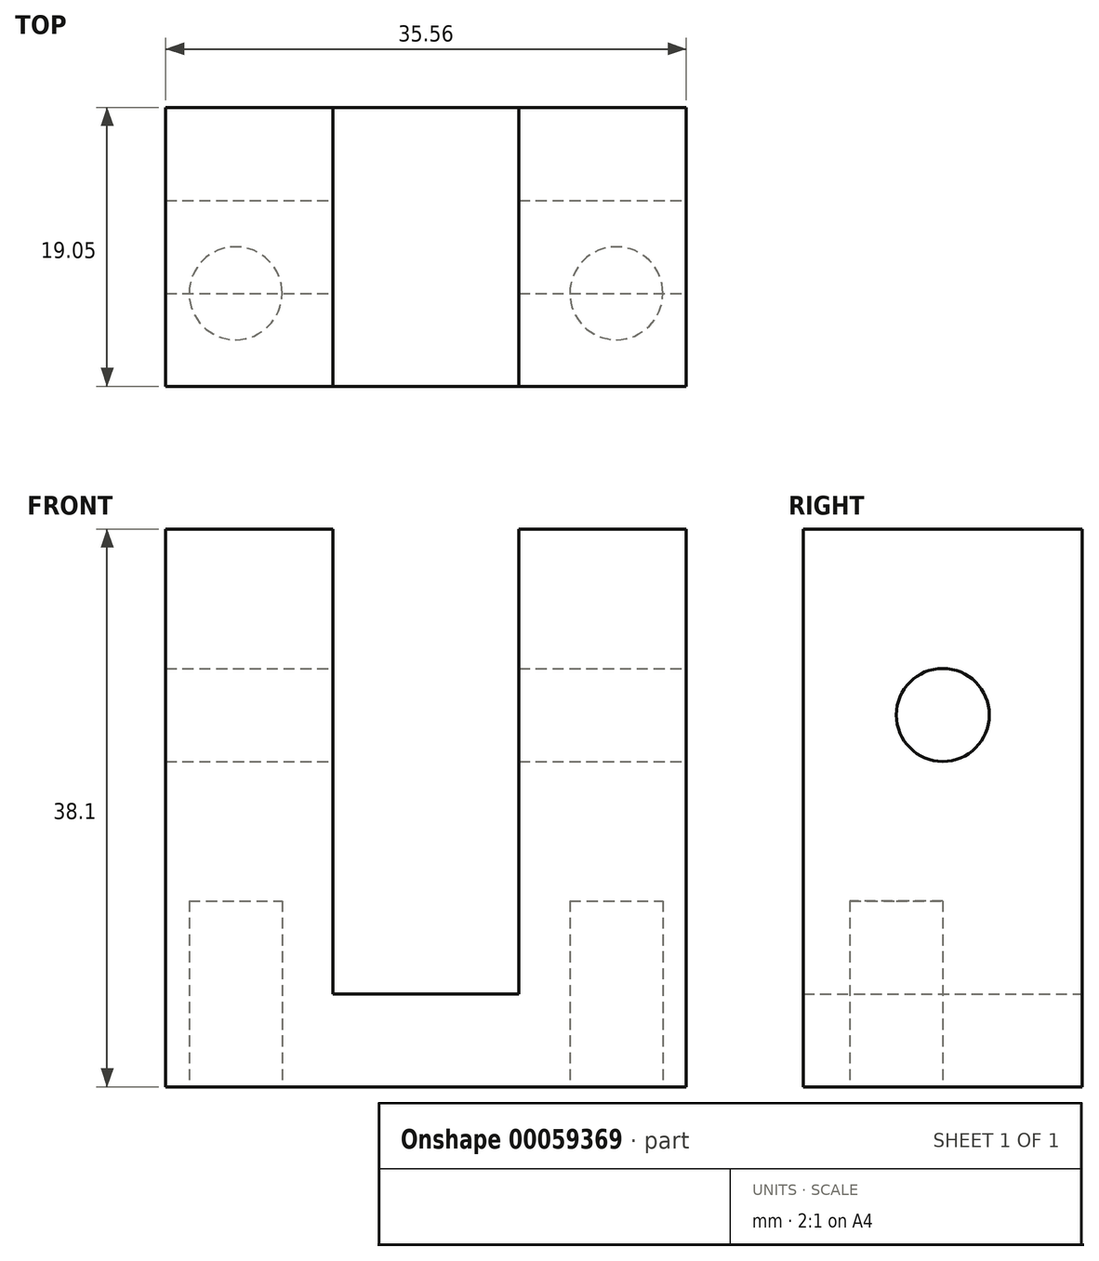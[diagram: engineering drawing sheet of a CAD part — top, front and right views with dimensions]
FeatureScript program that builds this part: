
annotation { "Feature Type Name" : "Feature", "Feature Type Description" : "" }
export const myFeature = defineFeature(function(context is Context, id is Id, definition is map)
    precondition{}
    {
        {
            var Q0;
            Q0=qCreatedBy(makeId("Front.planeOp"),FACE);
            var sketch = newSketch(context, id + "F0", { "sketchPlane" : qUnion([Q0])});
            skLineSegment(sketch, "E0", {"start": v(0, 0) * mm, "end": v(0, 38.1) * mm});
            skLineSegment(sketch, "E1", {"start": v(0, 38.1) * mm, "end": v(11.43, 38.1) * mm});
            skLineSegment(sketch, "E2", {"start": v(11.43, 38.1) * mm, "end": v(11.43, 6.35) * mm});
            skLineSegment(sketch, "E3", {"start": v(11.43, 6.35) * mm, "end": v(24.13, 6.35) * mm});
            skLineSegment(sketch, "E4", {"start": v(24.13, 6.35) * mm, "end": v(24.13, 38.1) * mm});
            skLineSegment(sketch, "E5", {"start": v(24.13, 38.1) * mm, "end": v(35.56, 38.1) * mm});
            skLineSegment(sketch, "E6", {"start": v(35.56, 38.1) * mm, "end": v(35.56, 0) * mm});
            skLineSegment(sketch, "E7", {"start": v(35.56, 0) * mm, "end": v(0, 0) * mm});
            skSolve(sketch);
        }
        {
            var Q0;
            Q0=makeQuery(id+"F0.imprint","IMPRINT",FACE,{"disambiguationData":[TD([[makeQuery(id+"F0.imprint","IMPRINT",EDGE,{"derivedFrom":sQuery(id+"F0.wireOp",EDGE,"E0")}),-1.0]])]});
            extrude(context, id + "F1", {"entities" : qUnion([Q0]), "depth" : 19.05 * mm});
        }
        {
            var Q0;
            Q0=makeQuery(id+"F1.opExtrude","SWEPT_FACE",FACE,{"disambiguationData":[OSD([sQuery(id+"F0.wireOp",EDGE,"E6")])]});
            var sketch = newSketch(context, id + "F2", { "sketchPlane" : qUnion([Q0])});
            skLineSegment(sketch, "E8", {"start": v(-9.53, 51.4) * mm, "end": v(-9.53, -7.93) * mm, "construction": true});
            skCircle(sketch, "E9", {"center": v(-9.53, 25.4) * mm, "radius": 3.18 * mm});
            skSolve(sketch);
        }
        {
            var Q0;
            Q0=makeQuery(id+"F2.imprint","IMPRINT",FACE,{"disambiguationData":[TD([[makeQuery(id+"F2.imprint","IMPRINT",EDGE,{"derivedFrom":sQuery(id+"F2.wireOp",EDGE,"E9")}),1.0]])]});
            extrude(context, id + "F3", {"entities" : qUnion([Q0]), "operationType" : NewBodyOperationType.REMOVE, "oppositeDirection" : true, "depth" : 1270 * mm});
        }
        {
            var Q0;
            Q0=makeQuery(id+"F1.opExtrude","SWEPT_FACE",FACE,{"disambiguationData":[OSD([sQuery(id+"F0.wireOp",EDGE,"E7")])]});
            var sketch = newSketch(context, id + "F4", { "sketchPlane" : qUnion([Q0])});
            skCircle(sketch, "E10", {"center": v(4.78, 12.7) * mm, "radius": 3.18 * mm});
            skCircle(sketch, "E11", {"center": v(30.78, 12.7) * mm, "radius": 3.18 * mm});
            skSolve(sketch);
        }
        {
            var Q0;
            Q0=makeQuery(id+"F4.imprint","IMPRINT",FACE,{"disambiguationData":[TD([[makeQuery(id+"F4.imprint","IMPRINT",EDGE,{"derivedFrom":sQuery(id+"F4.wireOp",EDGE,"E10")}),1.0]])]});
            var Q1;
            Q1=makeQuery(id+"F4.imprint","IMPRINT",FACE,{"disambiguationData":[TD([[makeQuery(id+"F4.imprint","IMPRINT",EDGE,{"derivedFrom":sQuery(id+"F4.wireOp",EDGE,"E11")}),1.0]])]});
            extrude(context, id + "F5", {"entities" : qUnion([Q0, Q1]), "operationType" : NewBodyOperationType.REMOVE, "oppositeDirection" : true, "depth" : 12.7 * mm});
        }
    });
